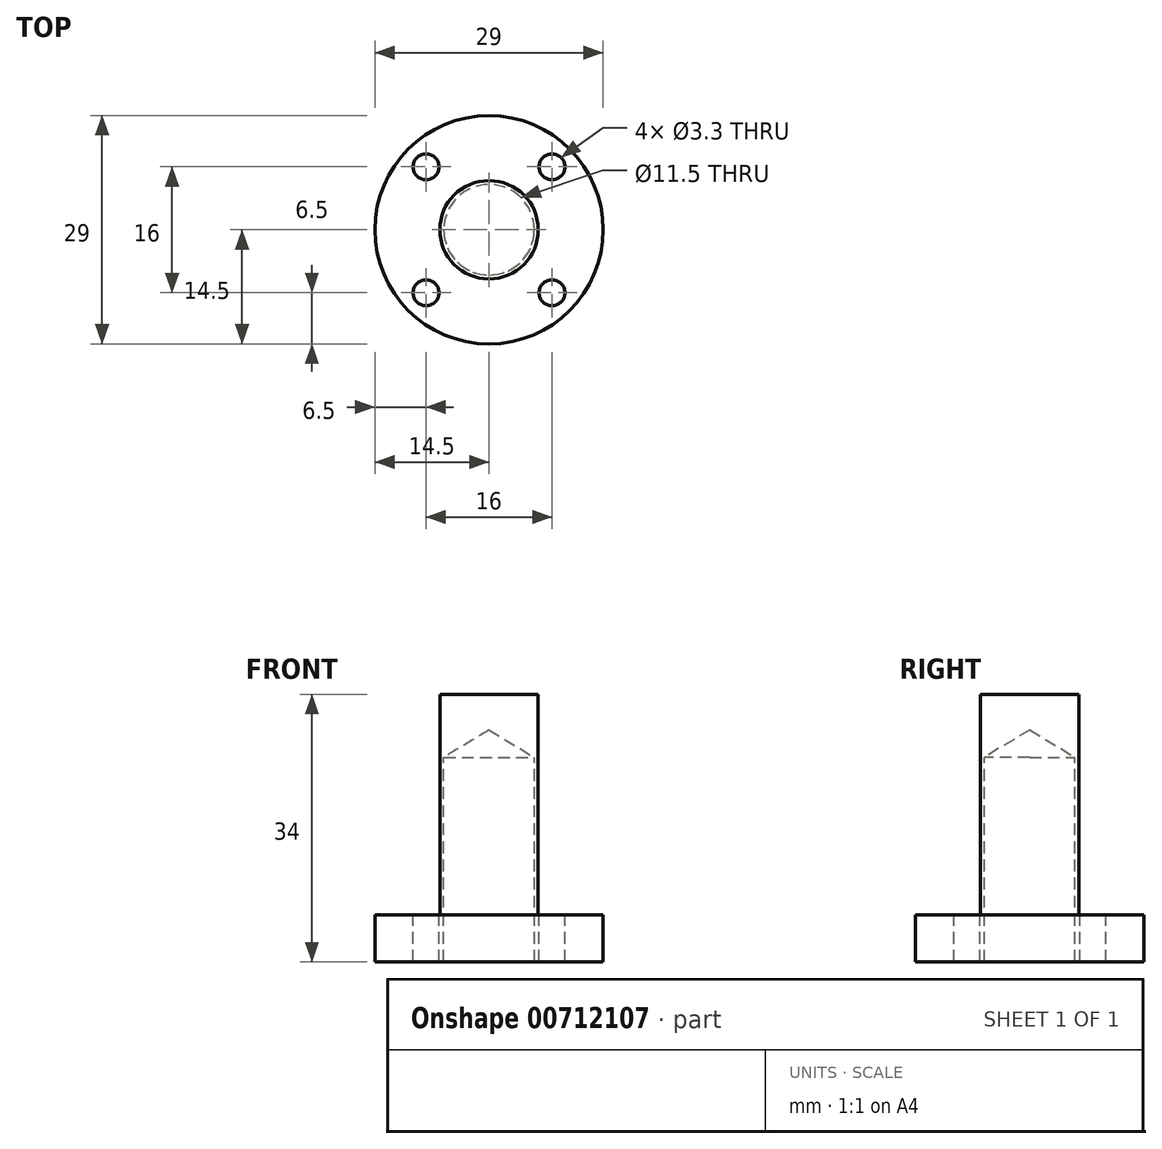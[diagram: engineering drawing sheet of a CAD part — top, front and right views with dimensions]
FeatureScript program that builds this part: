
annotation { "Feature Type Name" : "Feature", "Feature Type Description" : "" }
export const myFeature = defineFeature(function(context is Context, id is Id, definition is map)
    precondition{}
    {
        {
            var Q0;
            Q0=qCreatedBy(makeId("Top.planeOp"),FACE);
            var sketch = newSketch(context, id + "F0", { "sketchPlane" : qUnion([Q0])});
            skCircle(sketch, "E0", {"center": v(0, 0) * mm, "radius": 14.5 * mm});
            skCircle(sketch, "E1", {"center": v(0, 0) * mm, "radius": 6.25 * mm});
            skSolve(sketch);
        }
        {
            var Q0;
            Q0=makeQuery(id+"F0.imprint","IMPRINT",FACE,{"disambiguationData":[TD([[makeQuery(id+"F0.imprint","IMPRINT",EDGE,{"derivedFrom":sQuery(id+"F0.wireOp",EDGE,"E0")}),1.0]])]});
            var Q1;
            Q1=makeQuery(id+"F0.imprint","IMPRINT",FACE,{"disambiguationData":[TD([[makeQuery(id+"F0.imprint","IMPRINT",EDGE,{"derivedFrom":sQuery(id+"F0.wireOp",EDGE,"E1")}),1.0]])]});
            extrude(context, id + "F1", {"entities" : qUnion([Q0, Q1]), "oppositeDirection" : true, "depth" : 6 * mm, "offsetDistance" : 25 * mm});
        }
        {
            var Q0;
            Q0=makeQuery(id+"F0.imprint","IMPRINT",FACE,{"disambiguationData":[TD([[makeQuery(id+"F0.imprint","IMPRINT",EDGE,{"derivedFrom":sQuery(id+"F0.wireOp",EDGE,"E1")}),1.0]])]});
            extrude(context, id + "F2", {"entities" : qUnion([Q0]), "operationType" : NewBodyOperationType.ADD, "depth" : 28 * mm, "offsetDistance" : 25 * mm});
        }
        {
            var Q0;
            Q0=makeQuery(id+"F1.opExtrude","CAP_FACE",FACE,{"disambiguationData":[OSD([sQuery(id+"F0.wireOp",EDGE,"E0")])],"isStart":false});
            var sketch = newSketch(context, id + "F3", { "sketchPlane" : qUnion([Q0])});
            skLineSegment(sketch, "E2", {"start": v(0, 25.82) * mm, "end": v(0, -24.4) * mm, "construction": true});
            skLineSegment(sketch, "E3", {"start": v(20.47, 0) * mm, "end": v(-22.27, 0) * mm, "construction": true});
            skLineSegment(sketch, "E4.0", {"start": v(20.47, 8) * mm, "end": v(-22.27, 8) * mm, "construction": true});
            skLineSegment(sketch, "E5.0", {"start": v(20.47, -8) * mm, "end": v(-22.27, -8) * mm, "construction": true});
            skLineSegment(sketch, "E6.0", {"start": v(8, 25.82) * mm, "end": v(8, -24.4) * mm, "construction": true});
            skLineSegment(sketch, "E7.0", {"start": v(-8, 25.82) * mm, "end": v(-8, -24.4) * mm, "construction": true});
            skPoint(sketch, "E8", {"position": v(8, 8) * mm});
            skPoint(sketch, "E9", {"position": v(8, -8) * mm});
            skPoint(sketch, "E10", {"position": v(-8, -8) * mm});
            skPoint(sketch, "E11", {"position": v(-8, 8) * mm});
            skPoint(sketch, "E12", {"position": v(0, 0) * mm});
            skSolve(sketch);
        }
        {
            var Q0;
            Q0=sQuery(id+"F3.wireOp",VERTEX,"E8");
            var Q1;
            Q1=sQuery(id+"F3.wireOp",VERTEX,"E9");
            var Q2;
            Q2=sQuery(id+"F3.wireOp",VERTEX,"E10");
            var Q3;
            Q3=sQuery(id+"F3.wireOp",VERTEX,"E11");
            var Q4;
            Q4=makeQuery(id+"F1.opExtrude","SWEPT_BODY",BODY,{"disambiguationData":[OSD([sQuery(id+"F0.wireOp",EDGE,"E0")])]});
            hole(context, id + "F4", {"style" : HoleStyle.SIMPLE, "endStyle" : HoleEndStyle.THROUGH, "standardTappedOrClearance" : lookupTablePath({ "standard" : "ISO", "fit" : "Normal", "size" : "M3", "type" : "Clearance" }), "standardBlindInLast" : lookupTablePath({ "fit" : "Standard", "standard" : "ISO", "size" : "M3", "type" : "Clearance" }), "holeDiameter" : 3.3 * mm, "majorDiameter" : 5 * mm, "tappedDepth" : 12 * mm, "tapClearance" : 3, "locations" : qUnion([Q0, Q1, Q2, Q3]), "scope" : qUnion([Q4]), "startStyle" : HoleStartStyle.PART});
        }
        {
            var Q0;
            Q0=sQuery(id+"F3.wireOp",VERTEX,"E12");
            var Q1;
            Q1=makeQuery(id+"F1.opExtrude","SWEPT_BODY",BODY,{"disambiguationData":[OSD([sQuery(id+"F0.wireOp",EDGE,"E0")])]});
            hole(context, id + "F5", {"style" : HoleStyle.SIMPLE, "endStyle" : HoleEndStyle.BLIND, "holeDiameter" : 11.5 * mm, "majorDiameter" : 5 * mm, "holeDepth" : 26 * mm, "tappedDepth" : 12 * mm, "tapClearance" : 3, "locations" : qUnion([Q0]), "scope" : qUnion([Q1]), "startStyle" : HoleStartStyle.PART});
        }
    });
